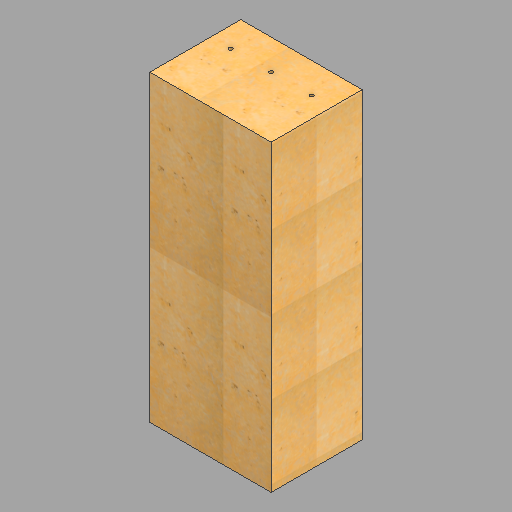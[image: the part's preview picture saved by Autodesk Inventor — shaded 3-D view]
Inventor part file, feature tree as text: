
AUTODESK INVENTOR PART (.ipt)
format: ipt  version: 2023 (Build 270158030, 158C)  size: 520,704 bytes
history: native  units: in
note: dims shown in document units (in); Inventor stores cm internally (conversion verified against a paired STEP export)
features: other x4, sketch x2, thicken_offset x2, projected_geometry x2, extrude x1
ambient origin geometry x8: Origin, YZ Plane, XZ Plane, XY Plane, X Axis, Y Axis, Z Axis, Center Point
bodies: Body1 (feature_tree)
feature tree (11):
  other  "Bottom"
  other  "Standard - Amber select"
  sketch  "Sketch1"  dims[d0=0.3937in d1=12.0in]
  thicken_offset  "Thicken1"
  thicken_offset  "Thicken2"
  extrude  "Extrusion1"  Depth=0.3937in
  other  "Bottom::Standard - Amber select"
  other  "TaggingFeature1"
  projected_geometry  "Projected Loop1"
  projected_geometry  "Projected Loop2"
  sketch  "Sketch2"  dims[d2=12.0in d3=12.0in d4=12.0in d5=12.0in d6=8.0in d7=16.0in d8=16.0in d9=8.0in d10=1.5in d11=12.5in d12=0.0in]
